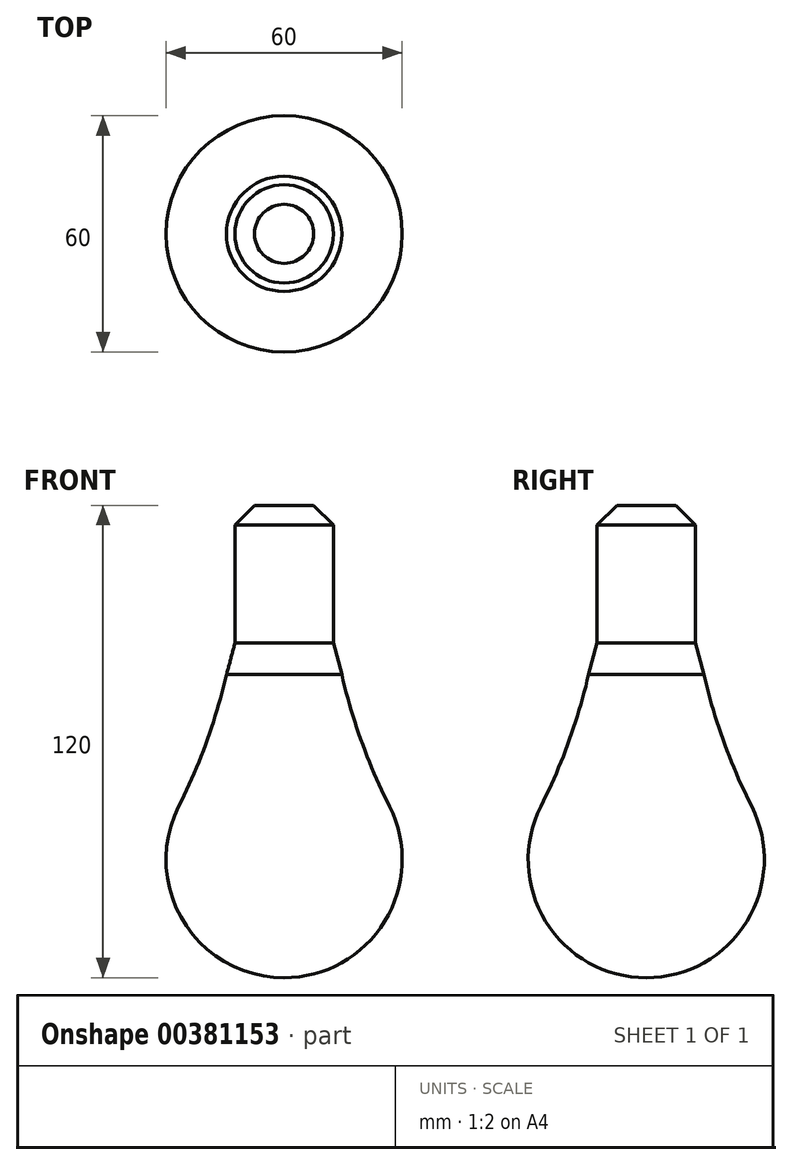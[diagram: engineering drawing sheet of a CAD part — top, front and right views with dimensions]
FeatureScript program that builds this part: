
annotation { "Feature Type Name" : "Feature", "Feature Type Description" : "" }
export const myFeature = defineFeature(function(context is Context, id is Id, definition is map)
    precondition{}
    {
        {
            var Q0;
            Q0=qCreatedBy(makeId("Front.planeOp"),FACE);
            var sketch = newSketch(context, id + "F0", { "sketchPlane" : qUnion([Q0])});
            skLineSegment(sketch, "E0", {"start": v(0, 0) * mm, "end": v(7.5, 0) * mm});
            skLineSegment(sketch, "E1", {"start": v(7.5, 0) * mm, "end": v(12.5, -5) * mm});
            skLineSegment(sketch, "E2", {"start": v(12.5, -5) * mm, "end": v(12.5, -35) * mm});
            skLineSegment(sketch, "E3", {"start": v(12.5, -35) * mm, "end": v(14.64, -43) * mm});
            skArc(sketch, "E4", {"start": v(14.64, -43) * mm, "mid": v(19.72, -60.11) * mm, "end": v(26.79, -76.5) * mm});
            skArc(sketch, "E5", {"start": v(0, -120) * mm, "mid": v(25.55, -105.73) * mm, "end": v(26.79, -76.5) * mm});
            skLineSegment(sketch, "E6", {"start": v(0, -120) * mm, "end": v(0, 0) * mm});
            skSolve(sketch);
        }
        {
            var Q0;
            Q0 = qSketchRegion(id + "F0", true);
            var Q1;
            Q1=sQuery(id+"F0.wireOp",EDGE,"E6");
            revolve(context, id + "F1", {"surfaceOperationType" : NewSurfaceOperationType.NEW, "entities" : qUnion([Q0]), "axis" : qUnion([Q1]), "revolveType" : RevolveType.FULL});
        }
    });
